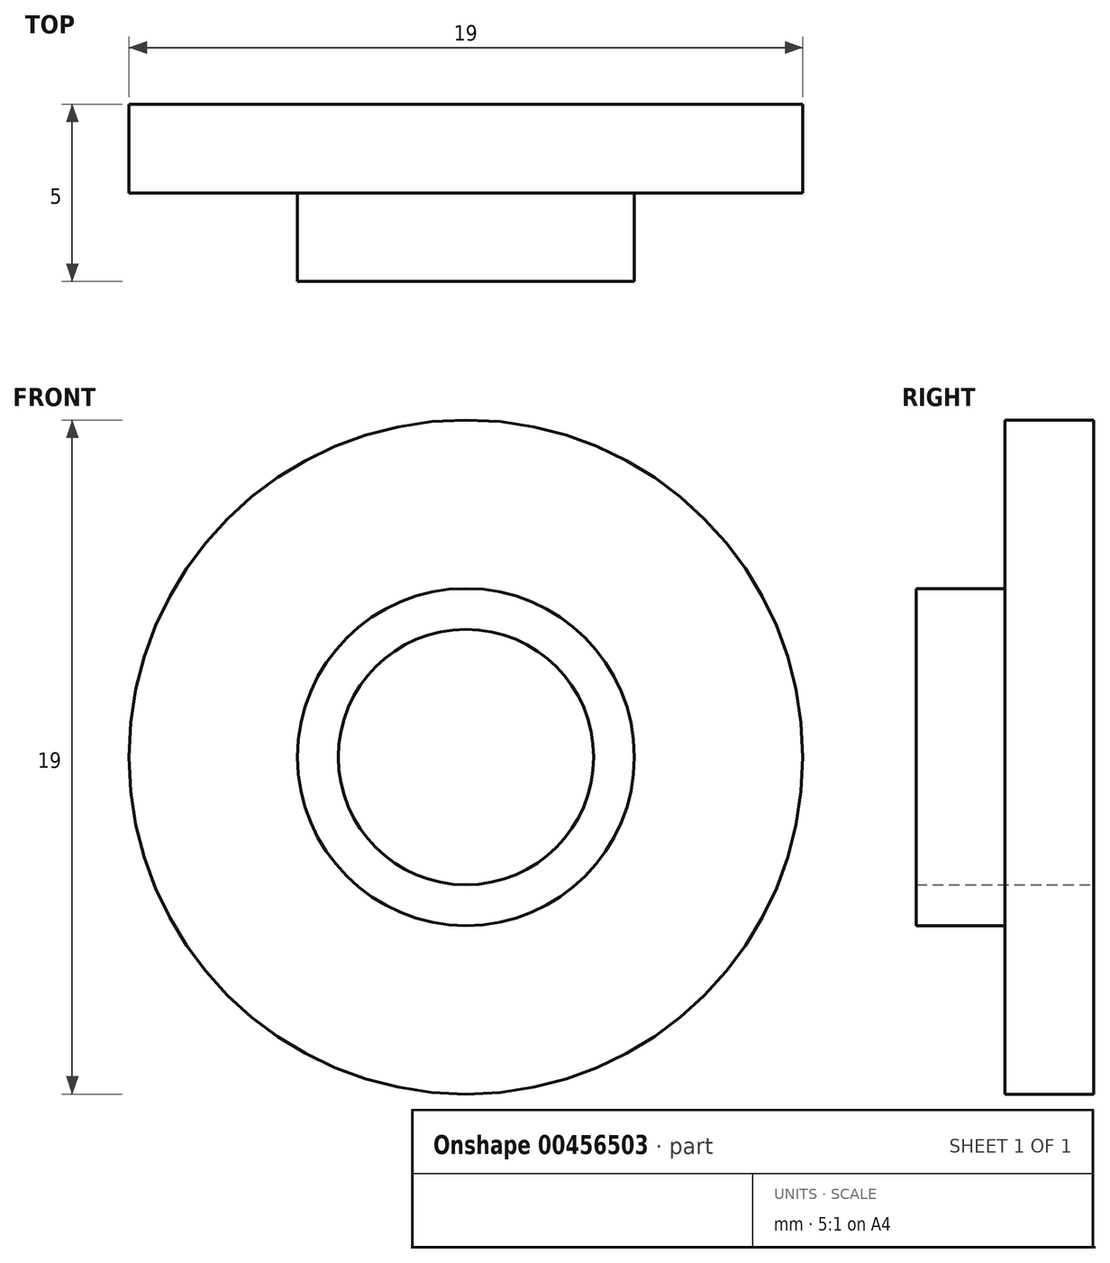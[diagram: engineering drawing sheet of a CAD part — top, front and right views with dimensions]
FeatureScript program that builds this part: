
annotation { "Feature Type Name" : "Feature", "Feature Type Description" : "" }
export const myFeature = defineFeature(function(context is Context, id is Id, definition is map)
    precondition{}
    {
        {
            var Q0;
            Q0=qCreatedBy(makeId("Front.planeOp"),FACE);
            var sketch = newSketch(context, id + "F0", { "sketchPlane" : qUnion([Q0])});
            skCircle(sketch, "E0", {"center": v(0, 0) * mm, "radius": 9.5 * mm});
            skSolve(sketch);
        }
        {
            var Q0;
            Q0 = qSketchRegion(id + "F0", true);
            extrude(context, id + "F1", {"entities" : qUnion([Q0]), "depth" : 2.5 * mm});
        }
        {
            var Q0;
            Q0=qCreatedBy(makeId("Front.planeOp"),FACE);
            var sketch = newSketch(context, id + "F2", { "sketchPlane" : qUnion([Q0])});
            skCircle(sketch, "E1", {"center": v(0, 0) * mm, "radius": 3.6 * mm});
            skSolve(sketch);
        }
        {
            var Q0;
            Q0=qCreatedBy(makeId("Front.planeOp"),FACE);
            var sketch = newSketch(context, id + "F3", { "sketchPlane" : qUnion([Q0])});
            skCircle(sketch, "E2", {"center": v(0, 0) * mm, "radius": 4.75 * mm});
            skSolve(sketch);
        }
        {
            var Q0;
            Q0 = qSketchRegion(id + "F3", true);
            extrude(context, id + "F4", {"entities" : qUnion([Q0]), "operationType" : NewBodyOperationType.ADD, "depth" : 5 * mm});
        }
        {
            var Q0;
            Q0 = qSketchRegion(id + "F2", true);
            extrude(context, id + "F5", {"entities" : qUnion([Q0]), "operationType" : NewBodyOperationType.REMOVE, "endBound" : BoundingType.THROUGH_ALL, "depth" : 25 * mm});
        }
    });
